# Revit family: Reece_Tap_Milli_Voir_Wall Telephone Bath Set
name_source: partatom
category: Plumbing Fixtures
revit_build: Autodesk Revit 2018 (Build: 20180329_1100(x64)
units: mm (PartAtom-declared; Revit-internal decimal feet)

## family parameters
Cut with Voids When Loaded = No
Host = Face
Part Type = Normal
Room Calculation Point = Yes
Round Connector Dimension = Use Diameter
Shared = Yes

## types (18) — shared parameters
Default Elevation = 1000 mm  [stored 3.28084 ft]
Reece_Backplate_Diameter = 55 mm
Reece_Detail_Additional = Wall Telephone Bath Set
Reece_Material_Colour = Reece_Porcelain_White
Reece_Product_Brand = Milli
Reece_Product_Mount = Wall Mounted
Reece_Product_Sub Brand = Voir
Reece_Product_Type = Tap
Reece_Product_Web Page = https://www.reece.com.au
Reece_Tap_Inlet = 12 mm  [stored 0.0393701 ft]
Reece_Tap_Reach = 253 mm
zero-valued in all types: CWFU, HWFU, WFU

## per-type parameters (varying)
| type | Reece_Material_Main | Reece_Material_Secondary | Reece_Mixer_Type | Reece_Product_Description | Reece_Product_Number |
| Brass Gold_Cross Handle | Reece_Brass_Gold | Reece_Brass_Gold | Reece_Tap_Milli_Voir_Wall Telephone Bath Set_Cross Handles_Standard_Nested | Milli Voir Wall Telephone Bath Set Cross Handles Polished Brass Gold (3 Star) | 2265355 |
| Brushed Nickel_Cross Handle | Reece_Brass_Brushed Nickel | Reece_Brass_Brushed Nickel | Reece_Tap_Milli_Voir_Wall Telephone Bath Set_Cross Handles_Standard_Nested | Milli Voir Wall Telephone Bath Set Cross Handles Brushed Nickel (3 Star) | 2265477 |
| Chrome_Cross Handle | Reece_Brass_Chrome | Reece_Brass_Chrome | Reece_Tap_Milli_Voir_Wall Telephone Bath Set_Cross Handles_Standard_Nested | Milli Voir Wall Telephone Bath Set Cross Handles Chrome (3 Star) | 2265294 |
| Matte Black_Cross Handle | Reece_Brass_Matte Black | Reece_Brass_Matte Black | Reece_Tap_Milli_Voir_Wall Telephone Bath Set_Cross Handles_Standard_Nested | Milli Voir Wall Telephone Bath Set Cross Handles Matte Black (3 Star) | 2265416 |
| Brass Gold_Lever Handle | Reece_Brass_Gold | Reece_Brass_Gold | Reece_Tap_Milli_Voir_Wall Telephone Bath Set_Lever Handles_Standard_Nested | Milli Voir Wall Telephone Bath Set Lever Handles Polished Brass Gold (3 Star) | 2265356 |
| Brushed Gunmetal_Lever Handle | Reece_Brass_Brushed Gunmetal | Reece_Brass_Brushed Gunmetal | Reece_Tap_Milli_Voir_Wall Telephone Bath Set_Lever Handles_Standard_Nested | Milli Voir Wall Telephone Bath Set Lever Handles Brushed Gunmetal (3 Star) | 2265539 |
| Brushed Nickel_Lever Handle | Reece_Brass_Brushed Nickel | Reece_Brass_Brushed Nickel |  | Milli Voir Wall Telephone Bath Set Lever Handles Brushed Nickel (3 Star) | 2265478 |
| Chrome_Lever Handle | Reece_Brass_Chrome | Reece_Brass_Chrome | Reece_Tap_Milli_Voir_Wall Telephone Bath Set_Lever Handles_Standard_Nested | Milli Voir Wall Telephone Bath Set Lever Handles Chrome (3 Star) | 2265295 |
| Matte Black_Lever Handle | Reece_Brass_Matte Black | Reece_Brass_Matte Black | Reece_Tap_Milli_Voir_Wall Telephone Bath Set_Lever Handles_Standard_Nested | Milli Voir Wall Telephone Bath Set Lever Handles Matte Black (3 Star) | 2265417 |
| Brass Gold_Lever Handle_Porcelain | Reece_Brass_Gold | Reece_Porcelain_White | Reece_Tap_Milli_Voir_Wall Telephone Bath Set_Lever Handles_Porcelain_Nested | Milli Voir Wall Telephone Bath Set Lever Porcelain Handles Polished Brass Gold (3 Star) | 2265357 |
| Brushed Gunmetal_Lever Handle_Porcelain | Reece_Brass_Brushed Gunmetal | Reece_Porcelain_White | Reece_Tap_Milli_Voir_Wall Telephone Bath Set_Lever Handles_Porcelain_Nested | Milli Voir Wall Telephone Bath Set Lever Porcelain Handles Brushed Gunmetal (3 Star) | 2265540 |
| Brushed Nickel_Lever Handle_Porcelain | Reece_Brass_Brushed Nickel | Reece_Porcelain_White | Reece_Tap_Milli_Voir_Wall Telephone Bath Set_Lever Handles_Porcelain_Nested | Milli Voir Wall Telephone Bath Set Lever Porcelain Handles Brushed Nickel (3 Star) | 2265479 |
| Chrome_Lever Handle_Porcelain | Reece_Brass_Chrome | Reece_Porcelain_White | Reece_Tap_Milli_Voir_Wall Telephone Bath Set_Lever Handles_Porcelain_Nested | Milli Voir Wall Telephone Bath Set Lever Porcelain Handles Chrome (3 Star) | 2265296 |
| Matte Black_Lever Handle_Porcelain | Reece_Brass_Matte Black | Reece_Porcelain_White | Reece_Tap_Milli_Voir_Wall Telephone Bath Set_Lever Handles_Porcelain_Nested | Milli Voir Wall Telephone Bath Set Lever Porcelain Handles Matte Black (3 Star) | 2265418 |
| Brushed Gunmetal_Cross Handle | Reece_Brass_Brushed Gunmetal | Reece_Brass_Brushed Gunmetal | Reece_Tap_Milli_Voir_Wall Telephone Bath Set_Cross Handles_Standard_Nested | Milli Voir Wall Telephone Bath Set Cross Handles Brushed Gunmetal (3 Star) | 2265538 |
| Brushed Gold_Cross Handle | Reece_Brass_Brushed Gold | Reece_Brass_Brushed Gold | Reece_Tap_Milli_Voir_Wall Telephone Bath Set_Cross Handles_Standard_Nested | Milli Voir Wall Mounted Telephone Bath Set Cross Handles Brushed Gold (3 Star) | 2266225 |
| Brushed Gold_Lever Handle | Reece_Brass_Brushed Gold | Reece_Brass_Brushed Gold | Reece_Tap_Milli_Voir_Wall Telephone Bath Set_Lever Handles_Standard_Nested | Milli Voir Wall Mounted Telephone Bath Set Lever Brushed Gold (3 Star) | 2266226 |
| Brushed Gold_Lever Handle_Porcelain | Reece_Brass_Brushed Gold | Reece_Porcelain_White | Reece_Tap_Milli_Voir_Wall Telephone Bath Set_Lever Handles_Porcelain_Nested | Milli Voir Wall Mounted Telephone Bath Set Lever Porcelain Handles Brushed Gold (3 Star) | 2266227 |

note: [stored X ft] marks values corroborated as IEEE doubles in the binary element streams (Revit-internal decimal feet)

## geometry (parser evidence)
native form markers: Sweep x12
no freeform markers — native parametric forms only
